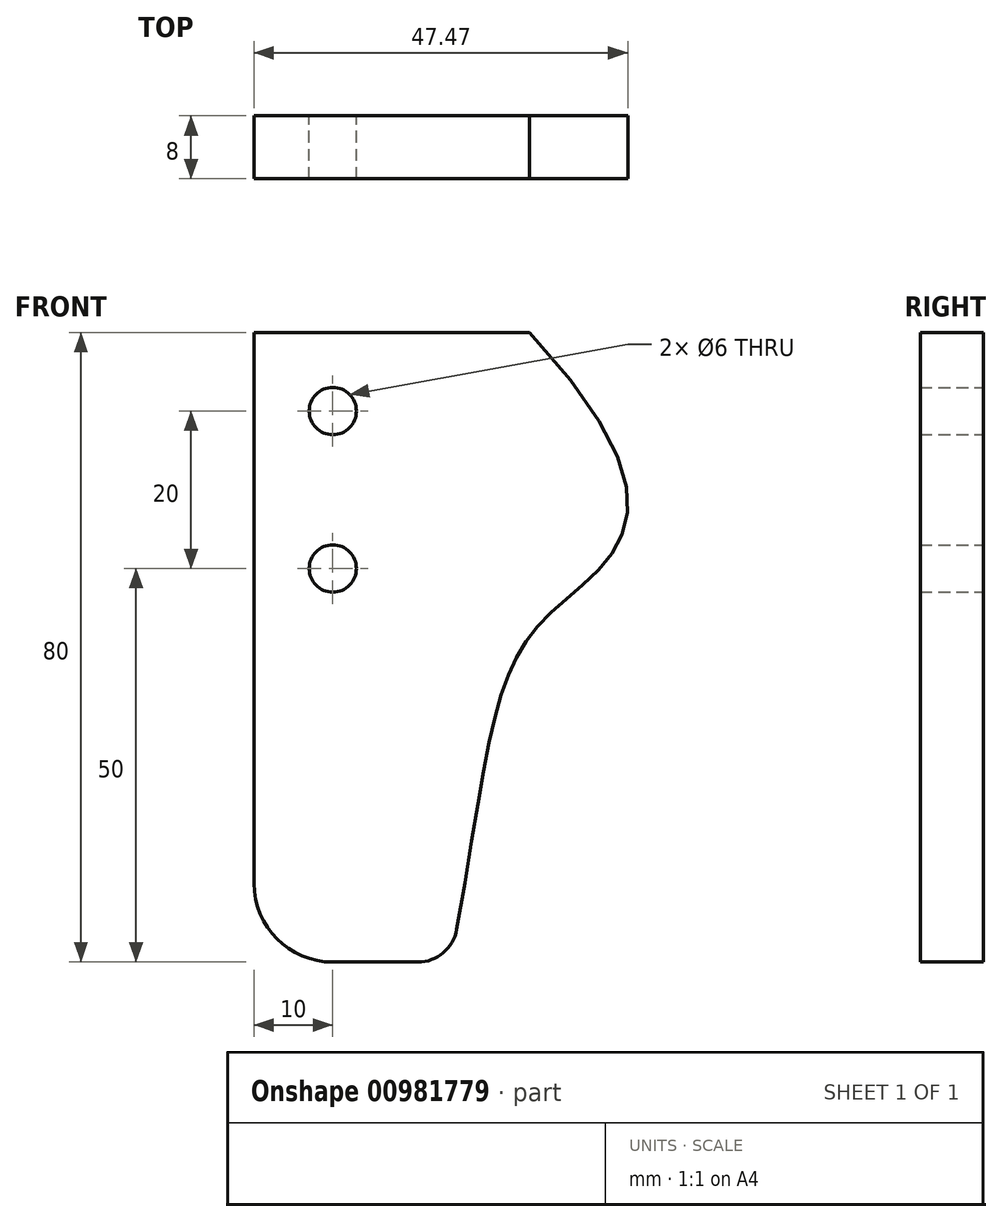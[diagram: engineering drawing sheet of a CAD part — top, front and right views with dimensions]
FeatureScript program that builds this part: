
annotation { "Feature Type Name" : "Feature", "Feature Type Description" : "" }
export const myFeature = defineFeature(function(context is Context, id is Id, definition is map)
    precondition{}
    {
        {
            var Q0;
            Q0=qCreatedBy(makeId("Front.planeOp"),FACE);
            var sketch = newSketch(context, id + "F0", { "sketchPlane" : qUnion([Q0])});
            skLineSegment(sketch, "E0.left", {"start": v(-150, 40) * mm, "end": v(-150, -40) * mm});
            skPoint(sketch, "E0.middle", {"position": v(0, 0) * mm});
            skCircle(sketch, "E1", {"center": v(-140, 30) * mm, "radius": 3 * mm});
            skCircle(sketch, "E2", {"center": v(-140, 10) * mm, "radius": 3 * mm});
            skLineSegment(sketch, "E3", {"start": v(-150, -40) * mm, "end": v(-125, -40) * mm});
            skLineSegment(sketch, "E4", {"start": v(-150, 40) * mm, "end": v(-115, 40) * mm});
            skFitSpline(sketch, "E5", {"points": [v(-125, -40) * mm, v(-112.45, 4.25) * mm, v(-115, 40) * mm], "startDerivative": vector(29.08, 159.73) * mm, "endDerivative": vector(-142.2, 153.62) * mm});
            skSolve(sketch);
        }
        {
            assignVariable(context, id + "F1", {"name" : "Plexiglas", "anyValue" : 8});
        }
        {
            var Q0;
            Q0=makeQuery(id+"F0.imprint","IMPRINT",FACE,{"disambiguationData":[TD([[makeQuery(id+"F0.imprint","IMPRINT",EDGE,{"derivedFrom":sQuery(id+"F0.wireOp",EDGE,"E0.left")}),1.0]])]});
            extrude(context, id + "F2", {"entities" : qUnion([Q0]), "depth" : (getVariable(context, 'Plexiglas')) * mm, "offsetDistance" : 25 * mm});
        }
        {
            var Q0;
            Q0=makeQuery(id+"F2.opExtrude","SWEPT_EDGE",EDGE,{"disambiguationData":[OSD([sQuery(id+"F0.wireOp",EDGE,"E0.left"),sQuery(id+"F0.wireOp",EDGE,"E3")])]});
            fillet(context, id + "F3", {"entities" : qUnion([Q0]), "radius" : 10 * mm, "tangentPropagation" : true, "allowEdgeOverflow" : false});
        }
        {
            var Q0;
            Q0=makeQuery(id+"F2.opExtrude","SWEPT_EDGE",EDGE,{"disambiguationData":[OSD([sQuery(id+"F0.wireOp",EDGE,"E3"),sQuery(id+"F0.wireOp",EDGE,"E5")])]});
            fillet(context, id + "F4", {"entities" : qUnion([Q0]), "radius" : 5 * mm, "tangentPropagation" : true, "allowEdgeOverflow" : false});
        }
    });
